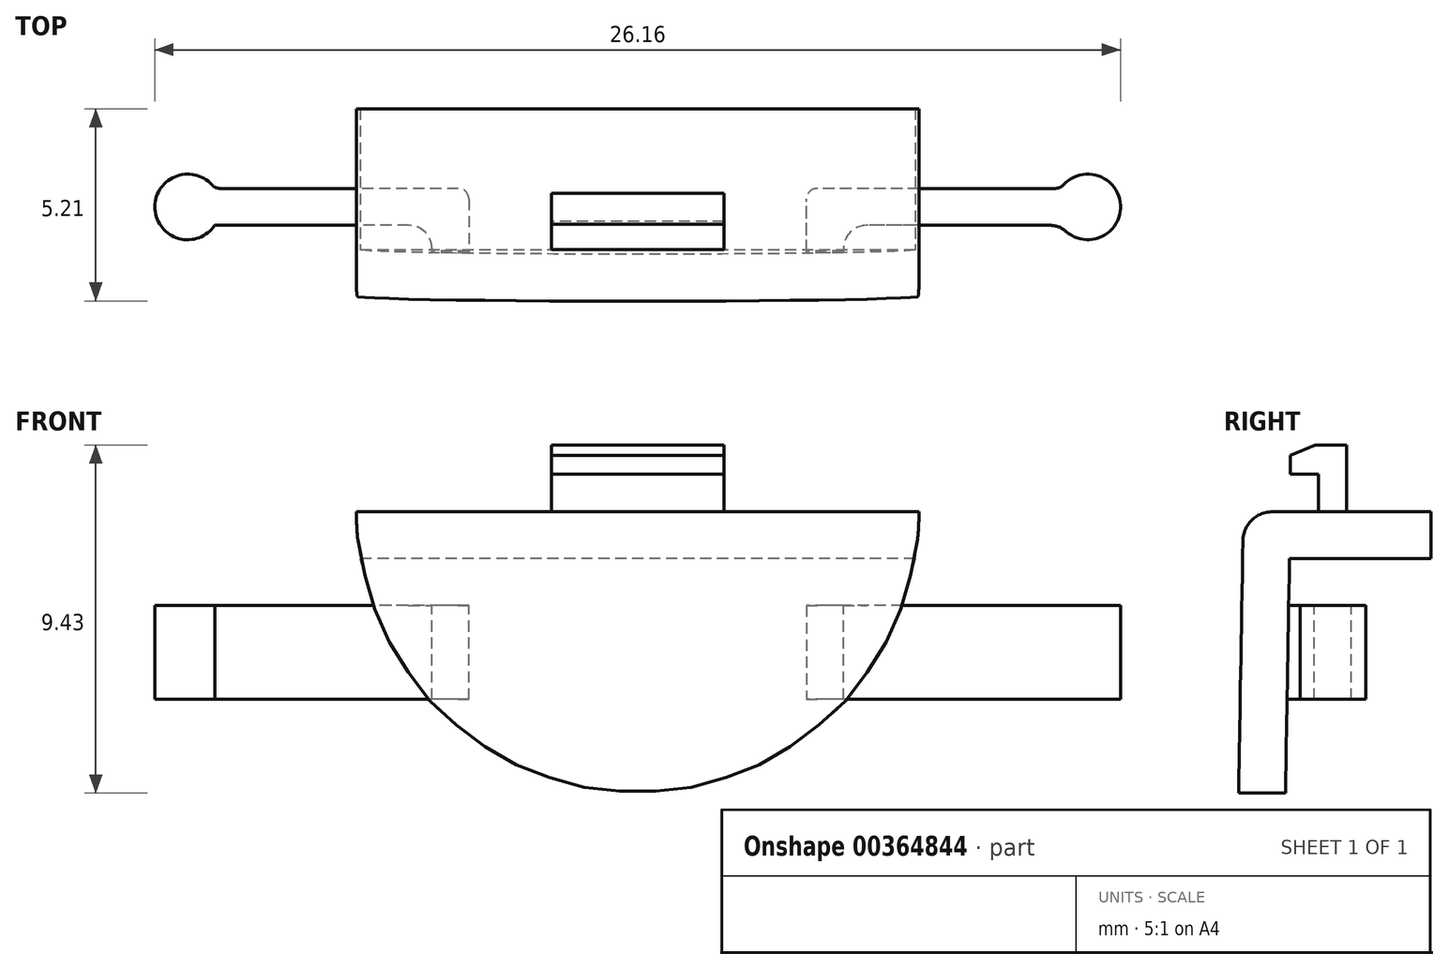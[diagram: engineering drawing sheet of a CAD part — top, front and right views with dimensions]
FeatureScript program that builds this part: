
annotation { "Feature Type Name" : "Feature", "Feature Type Description" : "" }
export const myFeature = defineFeature(function(context is Context, id is Id, definition is map)
    precondition{}
    {
        {
            var Q0;
            Q0=qCreatedBy(makeId("Right.planeOp"),FACE);
            var sketch = newSketch(context, id + "F0", { "sketchPlane" : qUnion([Q0])});
            skLineSegment(sketch, "E0.bottom", {"start": v(2.54, 3.8) * mm, "end": v(-2.54, 3.8) * mm});
            skLineSegment(sketch, "E0.top", {"start": v(2.54, -3.81) * mm, "end": v(-2.54, -3.81) * mm});
            skLineSegment(sketch, "E0.left", {"start": v(2.54, 3.81) * mm, "end": v(2.54, -3.81) * mm});
            skLineSegment(sketch, "E0.right", {"start": v(-2.54, 3.81) * mm, "end": v(-2.54, -3.81) * mm});
            skPoint(sketch, "E0.middle", {"position": v(0, 0) * mm});
            skLineSegment(sketch, "E1", {"start": v(-2.54, 3.81) * mm, "end": v(-2.67, -3.81) * mm});
            skLineSegment(sketch, "E2", {"start": v(-2.67, -3.81) * mm, "end": v(-2.54, -3.81) * mm});
            skSolve(sketch);
        }
        {
            var Q0;
            Q0=makeQuery(id+"F0.imprint","IMPRINT",FACE,{"disambiguationData":[TD([[makeQuery(id+"F0.imprint","IMPRINT",EDGE,{"derivedFrom":sQuery(id+"F0.wireOp",EDGE,"E0.bottom")}),1.0]])]});
            var Q1;
            Q1=makeQuery(id+"F0.imprint","IMPRINT",FACE,{"disambiguationData":[TD([[makeQuery(id+"F0.imprint","IMPRINT",EDGE,{"derivedFrom":sQuery(id+"F0.wireOp",EDGE,"E0.right")}),-1.0]])]});
            extrude(context, id + "F1", {"entities" : qUnion([Q0, Q1]), "endBound" : BoundingType.SYMMETRIC, "depth" : 17.78 * mm});
        }
        {
            var Q0;
            Q0=qCreatedBy(makeId("Front.planeOp"),FACE);
            var sketch = newSketch(context, id + "F2", { "sketchPlane" : qUnion([Q0])});
            skPoint(sketch, "E3.0", {"position": v(0, 3.81) * mm});
            skCircle(sketch, "E4", {"center": v(0, 3.81) * mm, "radius": 7.62 * mm});
            skLineSegment(sketch, "E5.bottom", {"start": v(15.27, -9.69) * mm, "end": v(-15.27, -9.69) * mm});
            skLineSegment(sketch, "E5.top", {"start": v(15.27, 17.3) * mm, "end": v(-15.27, 17.3) * mm});
            skLineSegment(sketch, "E5.left", {"start": v(15.27, -9.69) * mm, "end": v(15.27, 17.3) * mm});
            skLineSegment(sketch, "E5.right", {"start": v(-15.27, -9.69) * mm, "end": v(-15.27, 17.3) * mm});
            skSolve(sketch);
        }
        {
            var Q0;
            {var subQ1=sQuery(id+"F0.wireOp",EDGE,"E0.right");var subQ7=makeQuery(id+"F1.opExtrude","CAP_EDGE",EDGE,{"disambiguationData":[OSD([subQ1])],"isStart":true});Q0=makeQuery(id+"F2.imprint","IMPRINT",FACE,{"disambiguationData":[TD([[makeQuery(id+"F2.imprint","IMPRINT",EDGE,{"derivedFrom":subQ7}),1.0]])]});}
            var Q1;
            {var subQ1=sQuery(id+"F0.wireOp",EDGE,"E0.right");var subQ7=makeQuery(id+"F1.opExtrude","CAP_EDGE",EDGE,{"disambiguationData":[OSD([subQ1])],"isStart":false});Q1=makeQuery(id+"F2.imprint","IMPRINT",FACE,{"disambiguationData":[TD([[makeQuery(id+"F2.imprint","IMPRINT",EDGE,{"derivedFrom":subQ7}),-1.0]])]});}
            var Q2;
            Q2=makeQuery(id+"F2.imprint","IMPRINT",FACE,{"disambiguationData":[TD([[makeQuery(id+"F2.imprint","IMPRINT",EDGE,{"derivedFrom":sQuery(id+"F2.wireOp",EDGE,"E5.bottom")}),-1.0]])]});
            extrude(context, id + "F3", {"entities" : qUnion([Q0, Q1, Q2]), "operationType" : NewBodyOperationType.REMOVE, "endBound" : BoundingType.SYMMETRIC, "oppositeDirection" : true, "depth" : 25.4 * mm});
        }
        {
            var Q0;
            Q0=makeQuery(id+"F3.boolean.opBoolean","COPY",FACE,{"derivedFrom":makeQuery(id+"F3.opExtrude","SWEPT_FACE",FACE,{"disambiguationData":[OSD([sQuery(id+"F2.wireOp",EDGE,"E4")])]})});
            var Q1;
            {var subQ0=sQuery(id+"F0.wireOp",EDGE,"E0.left");Q1=makeQuery(id+"FrHiY4cY2tfIL87_1.boolean.opBoolean","MERGE",FACE,{"derivedFrom":[makeQuery(id+"F1.opExtrude","SWEPT_FACE",FACE,{"disambiguationData":[OSD([subQ0])]}),makeQuery(id+"FrHiY4cY2tfIL87_1.opExtrude","CAP_FACE",FACE,{"disambiguationData":[OSD([subQ0,sQuery(id+"F2.wireOp",EDGE,"E4"),sQuery(id+"F2MqpIoP3G9n5TR_1.wireOp",EDGE,"12qQDMW8-3MYm-vlFs-n7Bu-PmzH7K5CcIyO.bottom"),sQuery(id+"F2MqpIoP3G9n5TR_1.wireOp",EDGE,"12qQDMW8-3MYm-vlFs-n7Bu-PmzH7K5CcIyO.top"),sQuery(id+"F2MqpIoP3G9n5TR_1.wireOp",EDGE,"12qQDMW8-3MYm-vlFs-n7Bu-PmzH7K5CcIyO.left"),sQuery(id+"F2MqpIoP3G9n5TR_1.wireOp",EDGE,"12qQDMW8-3MYm-vlFs-n7Bu-PmzH7K5CcIyO.right")])],"isStart":true})]});}
            shell(context, id + "F4", {"entities" : qUnion([Q0, Q1]), "thickness" : 1.27 * mm});
        }
        {
            var Q0;
            Q0=makeQuery(id+"F1.opExtrude","SWEPT_FACE",FACE,{"disambiguationData":[OSD([sQuery(id+"F0.wireOp",EDGE,"E0.bottom")])]});
            var sketch = newSketch(context, id + "F5", { "sketchPlane" : qUnion([Q0])});
            skLineSegment(sketch, "E6.bottom", {"start": v(4.44, 1.68) * mm, "end": v(-4.45, 1.68) * mm});
            skLineSegment(sketch, "E6.top", {"start": v(4.44, -0.86) * mm, "end": v(-4.45, -0.86) * mm});
            skLineSegment(sketch, "E6.left", {"start": v(4.44, 1.68) * mm, "end": v(4.44, -0.86) * mm});
            skLineSegment(sketch, "E6.right", {"start": v(-4.45, 1.68) * mm, "end": v(-4.45, -0.86) * mm});
            skPoint(sketch, "E6.middle", {"position": v(0, 0.41) * mm});
            skPoint(sketch, "E6.middle.positionSnap0", {"position": v(0, 2.54) * mm});
            skPoint(sketch, "E6.centerSnap0", {"position": v(0, 2.54) * mm});
            skLineSegment(sketch, "E7.top", {"start": v(-3.17, 1.68) * mm, "end": v(3.17, 1.68) * mm});
            skLineSegment(sketch, "E7.left", {"start": v(-3.17, 0.41) * mm, "end": v(-3.17, 1.68) * mm});
            skLineSegment(sketch, "E7.right", {"start": v(3.18, 0.41) * mm, "end": v(3.18, 1.68) * mm});
            skPoint(sketch, "E8", {"position": v(0, 1.68) * mm});
            skLineSegment(sketch, "E9", {"start": v(3.18, 0.41) * mm, "end": v(-3.17, 0.41) * mm});
            skSolve(sketch);
        }
        {
            var Q0;
            Q0=makeQuery(id+"F4.opShell","OFFSET_FACE",FACE,{"disambiguationData":[OSD([sQuery(id+"F0.wireOp",EDGE,"E0.bottom")])]});
            var sketch = newSketch(context, id + "F6", { "sketchPlane" : qUnion([Q0])});
            skLineSegment(sketch, "E10.bottom", {"start": v(12.2, -0.38) * mm, "end": v(4.57, -0.38) * mm});
            skLineSegment(sketch, "E10.top", {"start": v(12.2, 0.62) * mm, "end": v(5.57, 0.62) * mm});
            skLineSegment(sketch, "E10.left", {"start": v(12.2, -0.38) * mm, "end": v(12.2, 0.62) * mm});
            skLineSegment(sketch, "E10.right", {"start": v(-12.2, -0.38) * mm, "end": v(-12.2, 0.62) * mm});
            skLineSegment(sketch, "E11", {"start": v(-5.57, 0.62) * mm, "end": v(-5.57, 1.88) * mm});
            skLineSegment(sketch, "E12.trimOffspring", {"start": v(-5.57, 0.62) * mm, "end": v(-12.2, 0.62) * mm});
            skLineSegment(sketch, "E13.trimOffspring", {"start": v(-4.57, -0.38) * mm, "end": v(-12.2, -0.38) * mm});
            skLineSegment(sketch, "E14", {"start": v(-4.57, 1.88) * mm, "end": v(-5.57, 1.88) * mm});
            skCircle(sketch, "E15", {"center": v(-12.2, 0.12) * mm, "radius": 0.89 * mm});
            skCircle(sketch, "E16", {"center": v(12.2, 0.12) * mm, "radius": 0.89 * mm});
            skLineSegment(sketch, "E17", {"start": v(-4.57, -0.38) * mm, "end": v(-4.57, 1.88) * mm});
            skLineSegment(sketch, "E18", {"start": v(5.57, 0.62) * mm, "end": v(5.57, 1.88) * mm});
            skLineSegment(sketch, "E19", {"start": v(5.57, 1.88) * mm, "end": v(4.57, 1.88) * mm});
            skLineSegment(sketch, "E20", {"start": v(4.57, 1.88) * mm, "end": v(4.57, -0.38) * mm});
            skSolve(sketch);
        }
        {
            var Q0;
            {var subQ6=sQuery(id+"F6.wireOp",EDGE,"E12.trimOffspring");var subQ7=sQuery(id+"F6.wireOp",EDGE,"E11");var subQ8=makeQuery(id+"F6.imprint","INTERSECT",VERTEX,{"derivedFrom":[subQ7,subQ6]});Q0=makeQuery(id+"F6.imprint","IMPRINT",FACE,{"disambiguationData":[TD([[makeQuery(id+"F6.imprint","IMPRINT",EDGE,{"disambiguationData":[TD([[subQ8,-1.0]])],"derivedFrom":subQ6}),1.0]])]});}
            var Q1;
            {var subQ0=sQuery(id+"F6.wireOp",EDGE,"E15");var subQ1=sQuery(id+"F6.wireOp",EDGE,"E12.trimOffspring");var subQ2=makeQuery(id+"F6.imprint","INTERSECT",VERTEX,{"derivedFrom":[subQ1,subQ0]});Q1=makeQuery(id+"F6.imprint","IMPRINT",FACE,{"disambiguationData":[TD([[makeQuery(id+"F6.imprint","IMPRINT",EDGE,{"disambiguationData":[TD([[subQ2,1.0]])],"derivedFrom":subQ0}),-1.0]])]});}
            var Q2;
            {var subQ0=sQuery(id+"F6.wireOp",EDGE,"E10.right");Q2=makeQuery(id+"F6.imprint","IMPRINT",FACE,{"disambiguationData":[TD([[makeQuery(id+"F6.imprint","IMPRINT",EDGE,{"derivedFrom":subQ0}),-1.0]])]});}
            var Q3;
            {var subQ0=sQuery(id+"F6.wireOp",EDGE,"E10.right");Q3=makeQuery(id+"F6.imprint","IMPRINT",FACE,{"disambiguationData":[TD([[makeQuery(id+"F6.imprint","IMPRINT",EDGE,{"derivedFrom":subQ0}),1.0]])]});}
            var Q4;
            {var subQ9=sQuery(id+"F6.wireOp",EDGE,"E20");var subQ10=sQuery(id+"F6.wireOp",EDGE,"E10.bottom");var subQ11=makeQuery(id+"F6.imprint","INTERSECT",VERTEX,{"derivedFrom":[subQ10,subQ9]});Q4=makeQuery(id+"F6.imprint","IMPRINT",FACE,{"disambiguationData":[TD([[makeQuery(id+"F6.imprint","IMPRINT",EDGE,{"disambiguationData":[TD([[subQ11,1.0]])],"derivedFrom":subQ10}),-1.0]])]});}
            var Q5;
            {var subQ0=sQuery(id+"F6.wireOp",EDGE,"E16");var subQ1=sQuery(id+"F6.wireOp",EDGE,"E10.bottom");var subQ2=makeQuery(id+"F6.imprint","INTERSECT",VERTEX,{"derivedFrom":[subQ1,subQ0]});Q5=makeQuery(id+"F6.imprint","IMPRINT",FACE,{"disambiguationData":[TD([[makeQuery(id+"F6.imprint","IMPRINT",EDGE,{"disambiguationData":[TD([[subQ2,1.0]])],"derivedFrom":subQ0}),-1.0]])]});}
            var Q6;
            {var subQ0=sQuery(id+"F6.wireOp",EDGE,"E10.left");Q6=makeQuery(id+"F6.imprint","IMPRINT",FACE,{"disambiguationData":[TD([[makeQuery(id+"F6.imprint","IMPRINT",EDGE,{"derivedFrom":subQ0}),1.0]])]});}
            var Q7;
            {var subQ0=sQuery(id+"F6.wireOp",EDGE,"E10.left");Q7=makeQuery(id+"F6.imprint","IMPRINT",FACE,{"disambiguationData":[TD([[makeQuery(id+"F6.imprint","IMPRINT",EDGE,{"derivedFrom":subQ0}),-1.0]])]});}
            var Q8;
            {var subQ0=sQuery(id+"F6.wireOp",EDGE,"E14");Q8=makeQuery(id+"F6.imprint","IMPRINT",FACE,{"disambiguationData":[TD([[makeQuery(id+"F6.imprint","IMPRINT",EDGE,{"derivedFrom":subQ0}),1.0]])]});}
            var Q9;
            {var subQ0=sQuery(id+"F6.wireOp",EDGE,"E19");Q9=makeQuery(id+"F6.imprint","IMPRINT",FACE,{"disambiguationData":[TD([[makeQuery(id+"F6.imprint","IMPRINT",EDGE,{"derivedFrom":subQ0}),1.0]])]});}
            extrude(context, id + "F7", {"entities" : qUnion([Q0, Q1, Q2, Q3, Q4, Q5, Q6, Q7, Q8, Q9]), "operationType" : NewBodyOperationType.ADD, "depth" : 3.8 * mm, "hasSecondDirection" : true, "secondDirectionOppositeDirection" : false, "secondDirectionDepth" : 1.27 * mm});
        }
        {
            var Q0;
            Q0=makeQuery(id+"F7.opExtrude","SWEPT_EDGE",EDGE,{"disambiguationData":[OSD([sQuery(id+"F6.wireOp",EDGE,"E11"),sQuery(id+"F6.wireOp",EDGE,"E12.trimOffspring")])]});
            var Q1;
            Q1=makeQuery(id+"F7.opExtrude","SWEPT_EDGE",EDGE,{"disambiguationData":[OSD([sQuery(id+"F6.wireOp",EDGE,"E10.top"),sQuery(id+"F6.wireOp",EDGE,"OMAfyVC5-3x7q-5L3S-t3Ba-hfxiSSCMsjmI")])]});
            fillet(context, id + "F8", {"entities" : qUnion([Q0, Q1]), "radius" : 0.64 * mm, "tangentPropagation" : true, "allowEdgeOverflow" : false});
        }
        {
            var Q0;
            Q0=makeQuery(id+"F7.opExtrude","SWEPT_EDGE",EDGE,{"disambiguationData":[OSD([sQuery(id+"F6.wireOp",EDGE,"CbH2yE15-NqAO-YfZq-c6bS-IQ15tqH18fF9"),sQuery(id+"F6.wireOp",EDGE,"E13.trimOffspring")])]});
            var Q1;
            Q1=makeQuery(id+"F7.opExtrude","SWEPT_EDGE",EDGE,{"disambiguationData":[OSD([sQuery(id+"F6.wireOp",EDGE,"E10.bottom"),sQuery(id+"F6.wireOp",EDGE,"EDAq08Dq-3NNz-O5vJ-1kCi-hhSmzoxTklgt")])]});
            fillet(context, id + "F9", {"entities" : qUnion([Q0, Q1]), "radius" : (.25 + (1 / 25.4)) * mm, "tangentPropagation" : true, "allowEdgeOverflow" : false});
        }
        {
            var Q0;
            {var subQ15=sQuery(id+"F6.wireOp",EDGE,"CbH2yE15-NqAO-YfZq-c6bS-IQ15tqH18fF9");Q0=makeQuery(id+"F6.imprint","IMPRINT",FACE,{"disambiguationData":[TD([[makeQuery(id+"F6.imprint","IMPRINT",EDGE,{"derivedFrom":subQ15}),1.0]])]});}
            var sketch = newSketch(context, id + "F10", { "sketchPlane" : qUnion([Q0])});
            skLineSegment(sketch, "E21.bottom", {"start": v(-5.57, 1.27) * mm, "end": v(-4.5, 1.27) * mm});
            skLineSegment(sketch, "E21.left", {"start": v(-5.57, 1.27) * mm, "end": v(-5.6, 0.6) * mm});
            skLineSegment(sketch, "E21.right", {"start": v(-4.5, 1.27) * mm, "end": v(-4.57, -0.54) * mm});
            skLineSegment(sketch, "E22", {"start": v(-4.57, -0.54) * mm, "end": v(-12.24, 0.4) * mm});
            skLineSegment(sketch, "E23", {"start": v(-12.24, 0.4) * mm, "end": v(-12.12, 1.4) * mm});
            skLineSegment(sketch, "E24", {"start": v(-12.12, 1.4) * mm, "end": v(-5.6, 0.6) * mm});
            skCircle(sketch, "E25", {"center": v(-12.18, 0.9) * mm, "radius": 0.89 * mm});
            skSolve(sketch);
        }
        {
            var Q0;
            Q0=qCreatedBy(makeId("Right.planeOp"),FACE);
            var sketch = newSketch(context, id + "F11", { "sketchPlane" : qUnion([Q0])});
            skLineSegment(sketch, "E26.0", {"start": v(-0.5, 3.81) * mm, "end": v(0.25, 3.81) * mm});
            skLineSegment(sketch, "E27", {"start": v(0.25, 3.8) * mm, "end": v(0.25, 5.33) * mm});
            skLineSegment(sketch, "E28", {"start": v(0.25, 5.33) * mm, "end": v(-1.27, 5.33) * mm});
            skLineSegment(sketch, "E29", {"start": v(-1.27, 5.33) * mm, "end": v(-1.27, 4.83) * mm});
            skLineSegment(sketch, "E30", {"start": v(-1.27, 4.83) * mm, "end": v(-0.5, 4.83) * mm});
            skLineSegment(sketch, "E31", {"start": v(-0.5, 4.83) * mm, "end": v(-0.5, 3.8) * mm});
            skPoint(sketch, "E32.orphan", {"position": v(2.54, 3.8) * mm});
            skPoint(sketch, "E33.orphan", {"position": v(-2.54, 3.8) * mm});
            skLineSegment(sketch, "E34", {"start": v(-1.27, 5.33) * mm, "end": v(-0.6, 5.62) * mm});
            skLineSegment(sketch, "E35", {"start": v(-0.6, 5.62) * mm, "end": v(0.25, 5.62) * mm});
            skLineSegment(sketch, "E36", {"start": v(0.25, 5.62) * mm, "end": v(0.25, 5.33) * mm});
            skSolve(sketch);
        }
        {
            var Q0;
            Q0=makeQuery(id+"F11.imprint","IMPRINT",FACE,{"disambiguationData":[TD([[makeQuery(id+"F11.imprint","IMPRINT",EDGE,{"derivedFrom":sQuery(id+"F11.wireOp",EDGE,"E26.0")}),1.0]])]});
            var Q1;
            Q1=makeQuery(id+"F11.imprint","IMPRINT",FACE,{"disambiguationData":[TD([[makeQuery(id+"F11.imprint","IMPRINT",EDGE,{"derivedFrom":sQuery(id+"F11.wireOp",EDGE,"E28")}),-1.0]])]});
            extrude(context, id + "F12", {"entities" : qUnion([Q0, Q1]), "operationType" : NewBodyOperationType.ADD, "endBound" : BoundingType.SYMMETRIC, "depth" : 4.67 * mm});
        }
        {
            var Q0;
            Q0=makeQuery(id+"F1.opExtrude","SWEPT_EDGE",EDGE,{"disambiguationData":[OSD([sQuery(id+"F0.wireOp",EDGE,"E0.bottom"),sQuery(id+"F0.wireOp",EDGE,"E0.right"),sQuery(id+"F0.wireOp",EDGE,"E1")])]});
            fillet(context, id + "F13", {"entities" : qUnion([Q0]), "radius" : 0.76 * mm, "tangentPropagation" : true, "allowEdgeOverflow" : false});
        }
    });
